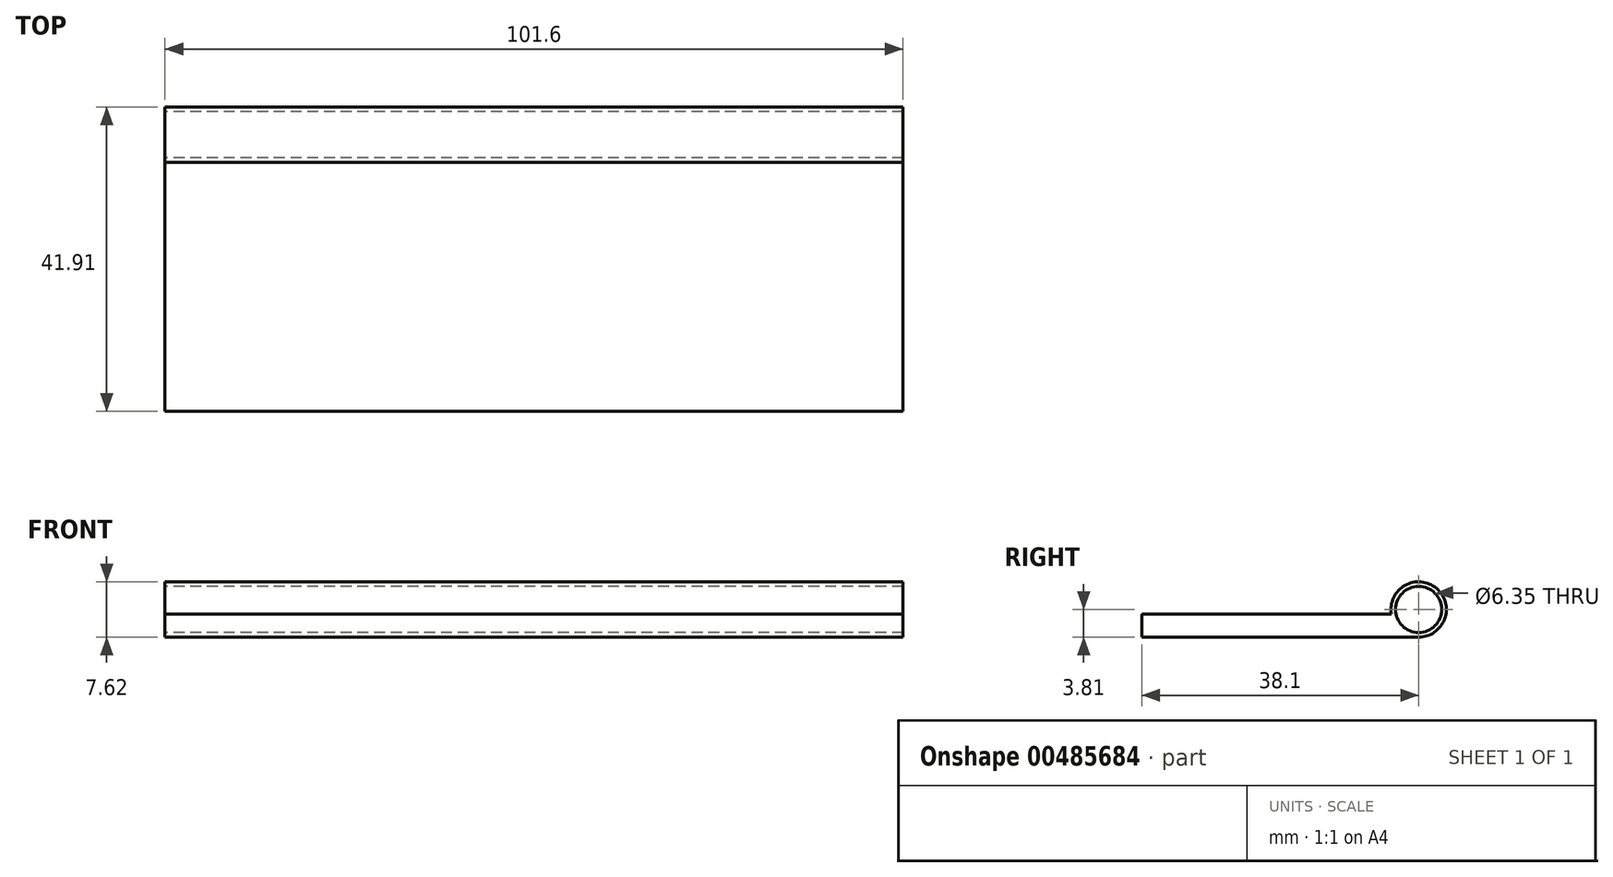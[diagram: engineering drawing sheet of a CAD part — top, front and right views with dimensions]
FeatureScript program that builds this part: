
annotation { "Feature Type Name" : "Feature", "Feature Type Description" : "" }
export const myFeature = defineFeature(function(context is Context, id is Id, definition is map)
    precondition{}
    {
        {
            var Q0;
            Q0=qCreatedBy(makeId("Top.planeOp"),FACE);
            var sketch = newSketch(context, id + "F0", { "sketchPlane" : qUnion([Q0])});
            skLineSegment(sketch, "E0.bottom", {"start": v(0, 0) * mm, "end": v(-101.6, 0) * mm});
            skLineSegment(sketch, "E0.top", {"start": v(0, -38.1) * mm, "end": v(-101.6, -38.1) * mm});
            skLineSegment(sketch, "E0.left", {"start": v(0, 0) * mm, "end": v(0, -38.1) * mm});
            skLineSegment(sketch, "E0.right", {"start": v(-101.6, 0) * mm, "end": v(-101.6, -38.1) * mm});
            skSolve(sketch);
        }
        {
            var Q0;
            Q0 = qSketchRegion(id + "F0", true);
            extrude(context, id + "F1", {"entities" : qUnion([Q0]), "depth" : 3.17 * mm});
        }
        {
            var Q0;
            Q0=makeQuery(id+"F1.opExtrude","SWEPT_FACE",FACE,{"disambiguationData":[OSD([sQuery(id+"F0.wireOp",EDGE,"E0.right")])]});
            var sketch = newSketch(context, id + "F2", { "sketchPlane" : qUnion([Q0])});
            skCircle(sketch, "E1", {"center": v(0, 3.81) * mm, "radius": 3.81 * mm});
            skCircle(sketch, "E2", {"center": v(0, 3.81) * mm, "radius": 3.18 * mm});
            skSolve(sketch);
        }
        {
            var Q0;
            {var subQ0=sQuery(id+"F2.wireOp",EDGE,"E1");var subQ1=sQuery(id+"F0.wireOp",EDGE,"E0.right");var subQ4=makeQuery(id+"F1.opExtrude","CAP_EDGE",EDGE,{"disambiguationData":[OSD([subQ1])],"isStart":false});var subQ5=makeQuery(id+"F2.imprint","INTERSECT",VERTEX,{"derivedFrom":[subQ4,subQ0]});Q0=makeQuery(id+"F2.imprint","IMPRINT",FACE,{"disambiguationData":[TD([[makeQuery(id+"F2.imprint","IMPRINT",EDGE,{"disambiguationData":[TD([[subQ5,1.0]])],"derivedFrom":subQ4}),1.0]])]});}
            var Q1;
            {var subQ0=sQuery(id+"F2.wireOp",EDGE,"E1");var subQ1=sQuery(id+"F0.wireOp",EDGE,"E0.right");var subQ4=makeQuery(id+"F1.opExtrude","CAP_EDGE",EDGE,{"disambiguationData":[OSD([subQ1])],"isStart":false});var subQ5=makeQuery(id+"F2.imprint","INTERSECT",VERTEX,{"derivedFrom":[subQ4,subQ0]});Q1=makeQuery(id+"F2.imprint","IMPRINT",FACE,{"disambiguationData":[TD([[makeQuery(id+"F2.imprint","IMPRINT",EDGE,{"disambiguationData":[TD([[subQ5,1.0]])],"derivedFrom":subQ4}),-1.0]])]});}
            var Q2;
            {var subQ0=sQuery(id+"F2.wireOp",EDGE,"E2");var subQ1=sQuery(id+"F0.wireOp",EDGE,"E0.right");var subQ4=makeQuery(id+"F1.opExtrude","CAP_EDGE",EDGE,{"disambiguationData":[OSD([subQ1])],"isStart":false});var subQ5=makeQuery(id+"F2.imprint","INTERSECT",VERTEX,{"derivedFrom":[subQ4,subQ0]});Q2=makeQuery(id+"F2.imprint","IMPRINT",FACE,{"disambiguationData":[TD([[makeQuery(id+"F2.imprint","IMPRINT",EDGE,{"disambiguationData":[TD([[subQ5,1.0]])],"derivedFrom":subQ0}),1.0]])]});}
            var Q3;
            Q3=makeQuery(id+"F1.opExtrude","SWEPT_FACE",FACE,{"disambiguationData":[OSD([sQuery(id+"F0.wireOp",EDGE,"E0.left")])]});
            extrude(context, id + "F3", {"entities" : qUnion([Q0, Q1, Q2]), "operationType" : NewBodyOperationType.REMOVE, "oppositeDirection" : true, "endBoundEntityFace" : qUnion([Q3]), "depth" : 254 * mm});
        }
        {
            var Q0;
            Q0 = qSketchRegion(id + "F2", true);
            var Q1;
            Q1=makeQuery(id+"F1.opExtrude","SWEPT_FACE",FACE,{"disambiguationData":[OSD([sQuery(id+"F0.wireOp",EDGE,"E0.left")])]});
            extrude(context, id + "F4", {"entities" : qUnion([Q0]), "operationType" : NewBodyOperationType.ADD, "endBound" : BoundingType.UP_TO_SURFACE, "oppositeDirection" : true, "endBoundEntityFace" : qUnion([Q1]), "depth" : 25.4 * mm});
        }
    });
